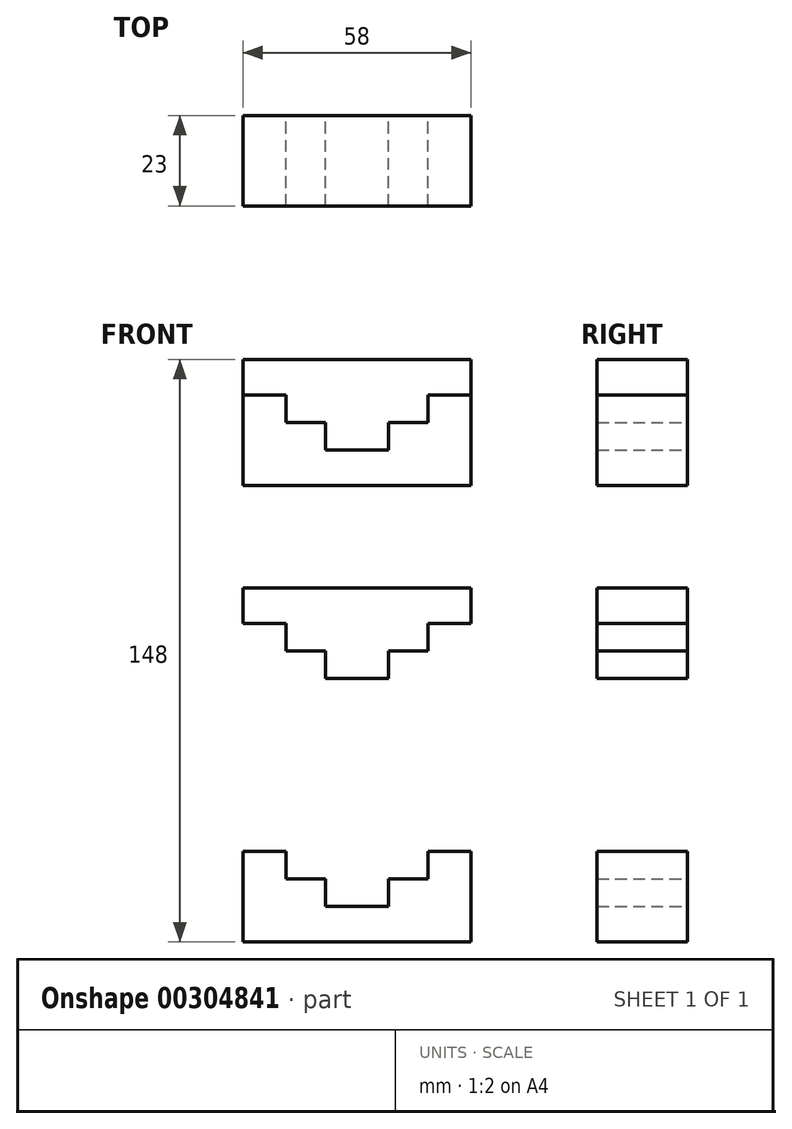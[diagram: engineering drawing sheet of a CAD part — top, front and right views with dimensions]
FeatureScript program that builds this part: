
annotation { "Feature Type Name" : "Feature", "Feature Type Description" : "" }
export const myFeature = defineFeature(function(context is Context, id is Id, definition is map)
    precondition{}
    {
        {
            var Q0;
            Q0=qCreatedBy(makeId("Front.planeOp"),FACE);
            var sketch = newSketch(context, id + "F0", { "sketchPlane" : qUnion([Q0])});
            skLineSegment(sketch, "E0.bottom", {"start": v(0, 0) * mm, "end": v(200, 0) * mm, "construction": true});
            skLineSegment(sketch, "E0.top", {"start": v(0, 300) * mm, "end": v(200, 300) * mm, "construction": true});
            skLineSegment(sketch, "E0.left", {"start": v(0, 0) * mm, "end": v(0, 300) * mm, "construction": true});
            skLineSegment(sketch, "E0.right", {"start": v(200, 0) * mm, "end": v(200, 300) * mm, "construction": true});
            skLineSegment(sketch, "E1.bottom", {"start": v(30, 270) * mm, "end": v(88, 270) * mm});
            skLineSegment(sketch, "E1.top", {"start": v(30, 247) * mm, "end": v(88, 247) * mm});
            skLineSegment(sketch, "E1.left", {"start": v(30, 270) * mm, "end": v(30, 247) * mm});
            skLineSegment(sketch, "E1.right", {"start": v(88, 270) * mm, "end": v(88, 247) * mm});
            skLineSegment(sketch, "E2.top", {"start": v(30, 293) * mm, "end": v(88, 293) * mm});
            skLineSegment(sketch, "E2.left", {"start": v(30, 270) * mm, "end": v(30, 293) * mm});
            skLineSegment(sketch, "E2.right", {"start": v(88, 270) * mm, "end": v(88, 293) * mm});
            skSolve(sketch);
        }
        {
            var Q0;
            Q0=qCreatedBy(makeId("Front.planeOp"),FACE);
            var sketch = newSketch(context, id + "F1", { "sketchPlane" : qUnion([Q0])});
            skLineSegment(sketch, "E3.bottom", {"start": v(30, 270) * mm, "end": v(41, 270) * mm});
            skLineSegment(sketch, "E3.top", {"start": v(30, 247) * mm, "end": v(88, 247) * mm});
            skLineSegment(sketch, "E3.left", {"start": v(30, 270) * mm, "end": v(30, 247) * mm});
            skLineSegment(sketch, "E3.right", {"start": v(88, 270) * mm, "end": v(88, 247) * mm});
            skPoint(sketch, "E4.endSnap0", {"position": v(59, 247) * mm});
            skLineSegment(sketch, "E5", {"start": v(59, 238.8) * mm, "end": v(59, 232.81) * mm, "construction": true});
            skLineSegment(sketch, "E6", {"start": v(41, 270) * mm, "end": v(41, 263) * mm});
            skLineSegment(sketch, "E7", {"start": v(41, 263) * mm, "end": v(51, 263) * mm});
            skLineSegment(sketch, "E8", {"start": v(51, 263) * mm, "end": v(51, 256) * mm});
            skLineSegment(sketch, "E9", {"start": v(51, 256) * mm, "end": v(59, 256) * mm});
            skLineSegment(sketch, "E10.MirrorCS", {"start": v(67, 256) * mm, "end": v(59, 256) * mm});
            skLineSegment(sketch, "E11.MirrorCS", {"start": v(67, 263) * mm, "end": v(67, 256) * mm});
            skLineSegment(sketch, "E12.MirrorCS", {"start": v(77, 263) * mm, "end": v(67, 263) * mm});
            skLineSegment(sketch, "E13.MirrorCS", {"start": v(77, 270) * mm, "end": v(77, 263) * mm});
            skLineSegment(sketch, "E14.top", {"start": v(30, 279) * mm, "end": v(88, 279) * mm});
            skLineSegment(sketch, "E14.left", {"start": v(30, 270) * mm, "end": v(30, 279) * mm});
            skLineSegment(sketch, "E14.right", {"start": v(88, 270) * mm, "end": v(88, 279) * mm});
            skLineSegment(sketch, "E15.trimOffspring", {"start": v(77, 270) * mm, "end": v(88, 270) * mm});
            skLineSegment(sketch, "E16.0.1.0", {"start": v(41, 205) * mm, "end": v(51, 205) * mm});
            skPoint(sketch, "E16.0.1.1", {"position": v(59, 189) * mm});
            skLineSegment(sketch, "E16.0.1.2", {"start": v(41, 212) * mm, "end": v(41, 205) * mm});
            skLineSegment(sketch, "E16.0.1.3", {"start": v(67, 205) * mm, "end": v(67, 198) * mm});
            skLineSegment(sketch, "E16.0.1.4", {"start": v(30, 212) * mm, "end": v(30, 189) * mm});
            skLineSegment(sketch, "E16.0.1.5", {"start": v(51, 205) * mm, "end": v(51, 198) * mm});
            skLineSegment(sketch, "E16.0.1.6", {"start": v(77, 205) * mm, "end": v(67, 205) * mm});
            skLineSegment(sketch, "E16.0.1.7", {"start": v(88, 212) * mm, "end": v(88, 189) * mm});
            skLineSegment(sketch, "E16.0.1.8", {"start": v(77, 212) * mm, "end": v(88, 212) * mm});
            skLineSegment(sketch, "E16.0.1.9", {"start": v(67, 198) * mm, "end": v(59, 198) * mm});
            skLineSegment(sketch, "E16.0.1.10", {"start": v(51, 198) * mm, "end": v(59, 198) * mm});
            skLineSegment(sketch, "E16.0.1.11", {"start": v(88, 212) * mm, "end": v(88, 221) * mm});
            skLineSegment(sketch, "E16.0.1.12", {"start": v(30, 221) * mm, "end": v(88, 221) * mm});
            skLineSegment(sketch, "E16.0.1.13", {"start": v(77, 212) * mm, "end": v(77, 205) * mm});
            skLineSegment(sketch, "E16.0.1.14", {"start": v(30, 212) * mm, "end": v(41, 212) * mm});
            skLineSegment(sketch, "E16.0.1.15", {"start": v(30, 212) * mm, "end": v(30, 221) * mm});
            skLineSegment(sketch, "E16.0.1.16", {"start": v(30, 189) * mm, "end": v(88, 189) * mm});
            skLineSegment(sketch, "E16.0.1.17", {"start": v(77, 212) * mm, "end": v(88, 212) * mm});
            skLineSegment(sketch, "E16.0.1.18", {"start": v(30, 212) * mm, "end": v(41, 212) * mm});
            skLineSegment(sketch, "E16.0.2.0", {"start": v(41, 147) * mm, "end": v(51, 147) * mm});
            skPoint(sketch, "E16.0.2.1", {"position": v(59, 131) * mm});
            skLineSegment(sketch, "E16.0.2.2", {"start": v(41, 154) * mm, "end": v(41, 147) * mm});
            skLineSegment(sketch, "E16.0.2.3", {"start": v(67, 147) * mm, "end": v(67, 140) * mm});
            skLineSegment(sketch, "E16.0.2.4", {"start": v(30, 154) * mm, "end": v(30, 131) * mm});
            skLineSegment(sketch, "E16.0.2.5", {"start": v(51, 147) * mm, "end": v(51, 140) * mm});
            skLineSegment(sketch, "E16.0.2.6", {"start": v(77, 147) * mm, "end": v(67, 147) * mm});
            skLineSegment(sketch, "E16.0.2.7", {"start": v(88, 154) * mm, "end": v(88, 131) * mm});
            skLineSegment(sketch, "E16.0.2.8", {"start": v(77, 154) * mm, "end": v(88, 154) * mm});
            skLineSegment(sketch, "E16.0.2.9", {"start": v(67, 140) * mm, "end": v(59, 140) * mm});
            skLineSegment(sketch, "E16.0.2.10", {"start": v(51, 140) * mm, "end": v(59, 140) * mm});
            skLineSegment(sketch, "E16.0.2.11", {"start": v(88, 154) * mm, "end": v(88, 163) * mm});
            skLineSegment(sketch, "E16.0.2.12", {"start": v(30, 163) * mm, "end": v(88, 163) * mm});
            skLineSegment(sketch, "E16.0.2.13", {"start": v(77, 154) * mm, "end": v(77, 147) * mm});
            skLineSegment(sketch, "E16.0.2.14", {"start": v(30, 154) * mm, "end": v(41, 154) * mm});
            skLineSegment(sketch, "E16.0.2.15", {"start": v(30, 154) * mm, "end": v(30, 163) * mm});
            skLineSegment(sketch, "E16.0.2.16", {"start": v(30, 131) * mm, "end": v(88, 131) * mm});
            skLineSegment(sketch, "E16.0.2.17", {"start": v(77, 154) * mm, "end": v(88, 154) * mm});
            skLineSegment(sketch, "E16.0.2.18", {"start": v(30, 154) * mm, "end": v(41, 154) * mm});
            skLineSegment(sketch, "E16.direction1", {"start": v(30, 247) * mm, "end": v(114.5, 247) * mm, "construction": true});
            skLineSegment(sketch, "E16.direction2", {"start": v(30, 247) * mm, "end": v(30, 189) * mm, "construction": true});
            skSolve(sketch);
        }
        {
            var Q0;
            Q0=makeQuery(id+"F1.imprint","IMPRINT",FACE,{"disambiguationData":[TD([[makeQuery(id+"F1.imprint","IMPRINT",EDGE,{"derivedFrom":sQuery(id+"F1.wireOp",EDGE,"E6")}),1.0]])]});
            var Q1;
            Q1=makeQuery(id+"F1.imprint","IMPRINT",FACE,{"disambiguationData":[TD([[makeQuery(id+"F1.imprint","IMPRINT",EDGE,{"derivedFrom":sQuery(id+"F1.wireOp",EDGE,"5c7086a2-823a-4756-8b90-18cd770687450.MirrorCS")}),-1.0]])]});
            var Q2;
            Q2=makeQuery(id+"F1.imprint","IMPRINT",FACE,{"disambiguationData":[TD([[makeQuery(id+"F1.imprint","IMPRINT",EDGE,{"derivedFrom":sQuery(id+"F1.wireOp",EDGE,"757c469c-bca3-4f06-9611-ba980f351d4e1.MirrorCS")}),1.0]])]});
            var Q3;
            Q3=makeQuery(id+"F1.imprint","IMPRINT",FACE,{"disambiguationData":[TD([[makeQuery(id+"F1.imprint","IMPRINT",EDGE,{"derivedFrom":sQuery(id+"F1.wireOp",EDGE,"E16.0.1.0")}),1.0]])]});
            var Q4;
            Q4=makeQuery(id+"F1.imprint","IMPRINT",FACE,{"disambiguationData":[TD([[makeQuery(id+"F1.imprint","IMPRINT",EDGE,{"derivedFrom":sQuery(id+"F1.wireOp",EDGE,"E16.0.2.0")}),-1.0]])]});
            extrude(context, id + "F2", {"entities" : qUnion([Q0, Q1, Q2, Q3, Q4]), "depth" : 23 * mm});
        }
        {
            var Q0;
            Q0=makeQuery(id+"F1.imprint","IMPRINT",FACE,{"disambiguationData":[TD([[makeQuery(id+"F1.imprint","IMPRINT",EDGE,{"derivedFrom":sQuery(id+"F1.wireOp",EDGE,"E3.top")}),1.0]])]});
            extrude(context, id + "F3", {"entities" : qUnion([Q0]), "depth" : 23 * mm});
        }
    });
